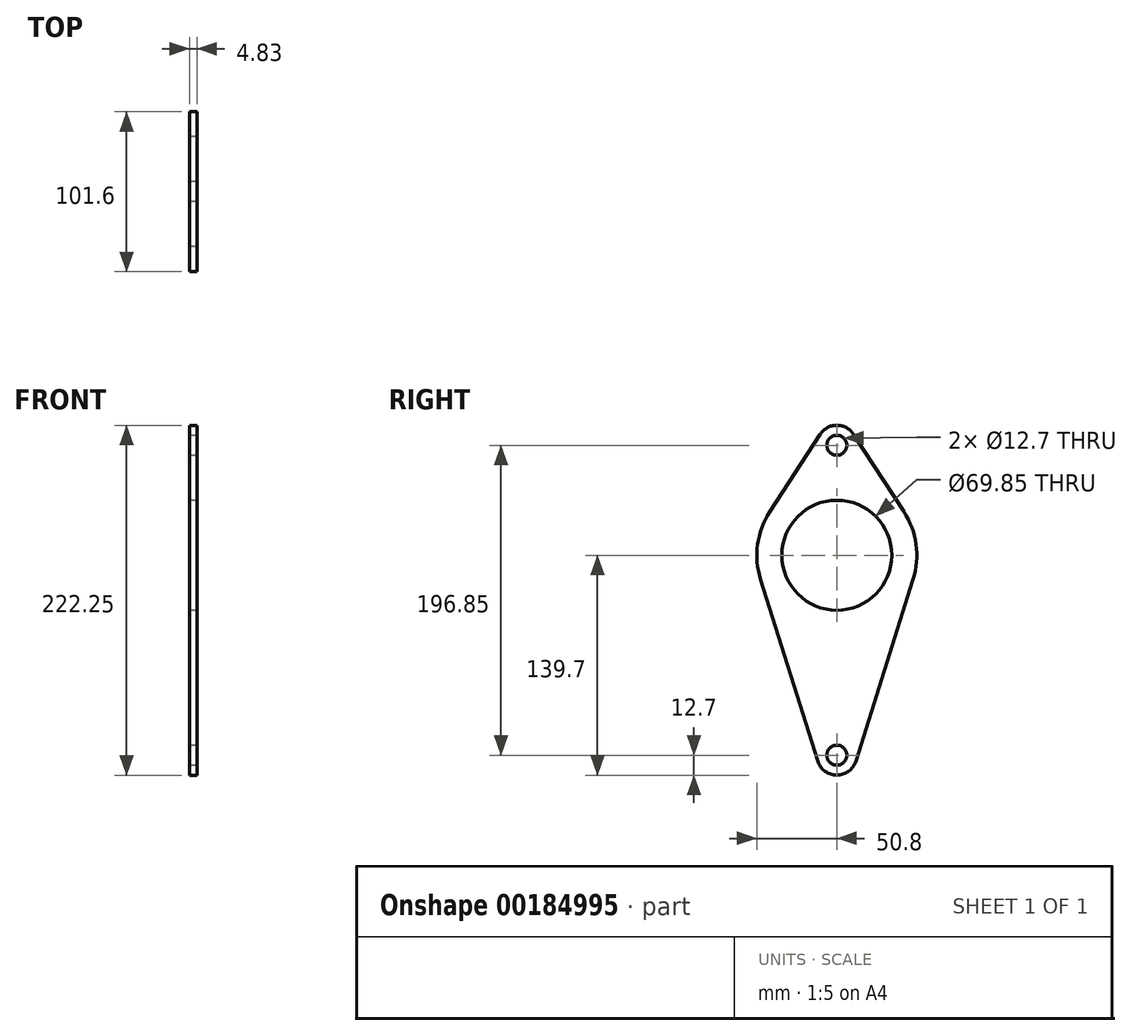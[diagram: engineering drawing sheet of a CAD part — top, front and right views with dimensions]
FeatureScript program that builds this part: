
annotation { "Feature Type Name" : "Feature", "Feature Type Description" : "" }
export const myFeature = defineFeature(function(context is Context, id is Id, definition is map)
    precondition{}
    {
        {
            var Q0;
            Q0=qCreatedBy(makeId("Right.planeOp"),FACE);
            var sketch = newSketch(context, id + "F0", { "sketchPlane" : qUnion([Q0])});
            skCircle(sketch, "E0", {"center": v(0, 0) * mm, "radius": 34.93 * mm});
            skArc(sketch, "E1", {"start": v(-42.58, 27.7) * mm, "mid": v(-50.33, 6.9) * mm, "end": v(-48.46, -15.24) * mm});
            skCircle(sketch, "E2", {"center": v(0, 69.85) * mm, "radius": 6.35 * mm});
            skCircle(sketch, "E3", {"center": v(0, -127) * mm, "radius": 6.35 * mm});
            skArc(sketch, "E4", {"start": v(10.64, 76.78) * mm, "mid": v(0, 82.55) * mm, "end": v(-10.64, 76.78) * mm});
            skArc(sketch, "E5", {"start": v(-12.12, -130.8) * mm, "mid": v(0, -139.7) * mm, "end": v(12.12, -130.8) * mm});
            skLineSegment(sketch, "E6", {"start": v(-48.46, -15.24) * mm, "end": v(-12.12, -130.8) * mm});
            skLineSegment(sketch, "E7", {"start": v(-10.64, 76.78) * mm, "end": v(-42.58, 27.7) * mm});
            skLineSegment(sketch, "E8", {"start": v(10.64, 76.78) * mm, "end": v(42.58, 27.7) * mm});
            skLineSegment(sketch, "E9", {"start": v(48.46, -15.24) * mm, "end": v(12.12, -130.8) * mm});
            skArc(sketch, "E10.trimOffspring", {"start": v(48.46, -15.24) * mm, "mid": v(50.33, 6.9) * mm, "end": v(42.58, 27.7) * mm});
            skSolve(sketch);
        }
        {
            var Q0;
            Q0=makeQuery(id+"F0.imprint","IMPRINT",FACE,{"disambiguationData":[TD([[makeQuery(id+"F0.imprint","IMPRINT",EDGE,{"derivedFrom":sQuery(id+"F0.wireOp",EDGE,"E0")}),-1.0]])]});
            extrude(context, id + "F1", {"entities" : qUnion([Q0]), "depth" : 4.83 * mm});
        }
    });
